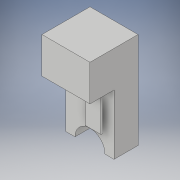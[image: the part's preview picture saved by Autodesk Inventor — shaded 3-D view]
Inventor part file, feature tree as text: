
AUTODESK INVENTOR PART (.ipt)
format: ipt  version: 2019 (Build 230136000, 136)  size: 128,000 bytes
history: native  units: in
note: dims shown in document units (in); Inventor stores cm internally (conversion verified against a paired STEP export)
features: extrude x4, sketch x4, other x1
ambient origin geometry x8: Origin, YZ Plane, XZ Plane, XY Plane, X Axis, Y Axis, Z Axis, Center Point
bodies: Body1 (feature_tree)
feature tree (9):
  other  "graber base"
  extrude  "Extrusion3"  Depth=2.0in
  extrude  "Extrusion4"  Depth=0.625in
  extrude  "Extrusion5"  Depth=2.0in
  extrude  "Extrusion6"  Depth=2.0in TaperAngle=0.0deg
  sketch  "Sketch4"  dims[d6=4.0in d7=2.0in]
  sketch  "Sketch5"  dims[d8=2.0in d9=0.0in d10=0.625in]
  sketch  "Sketch6"  dims[d11=1.25in d12=2.0in]
  sketch  "Sketch7"  dims[d13=0.375in d14=2.0in d15=0.0in d16=2.5in d17=0.0in d18=0.675in d19=0.075in d20=2.0in d21=0.1625in d22=0.3in d23=1.5in d24=0.0in]
